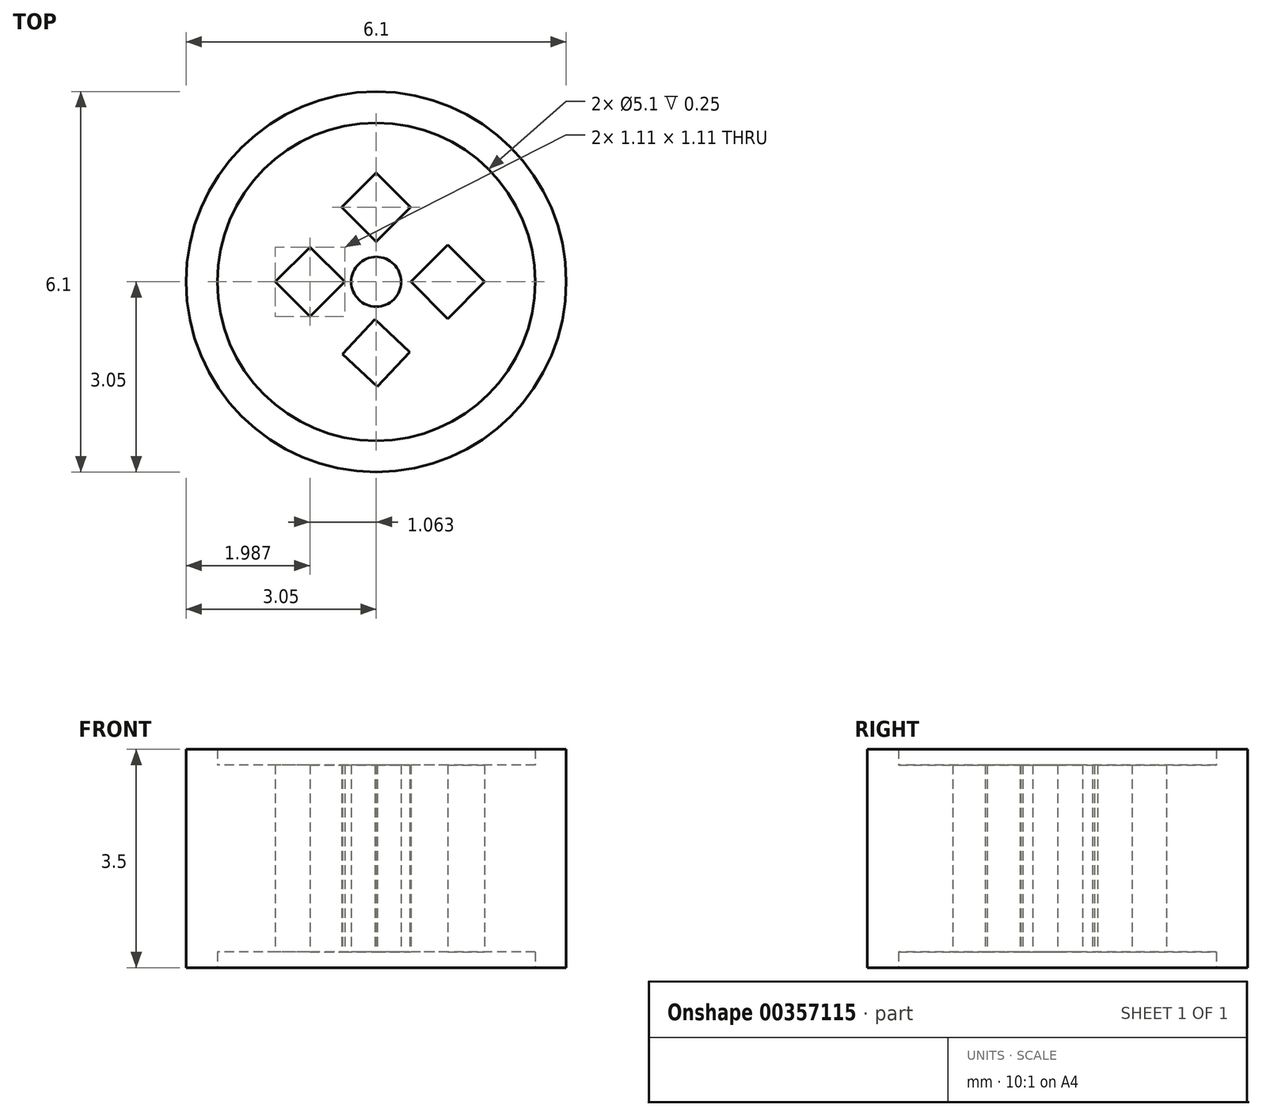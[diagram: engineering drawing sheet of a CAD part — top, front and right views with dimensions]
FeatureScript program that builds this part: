
annotation { "Feature Type Name" : "Feature", "Feature Type Description" : "" }
export const myFeature = defineFeature(function(context is Context, id is Id, definition is map)
    precondition{}
    {
        {
            var Q0;
            Q0=qCreatedBy(makeId("Top.planeOp"),FACE);
            var sketch = newSketch(context, id + "F0", { "sketchPlane" : qUnion([Q0])});
            skCircle(sketch, "E0", {"center": v(0, 0) * mm, "radius": 0.4 * mm});
            skCircle(sketch, "E1", {"center": v(0, 0) * mm, "radius": 2.55 * mm});
            skCircle(sketch, "E2", {"center": v(0, 0) * mm, "radius": 3.05 * mm});
            skLineSegment(sketch, "E3.0", {"start": v(-0.55, 1.2) * mm, "end": v(0, 1.75) * mm});
            skLineSegment(sketch, "E3.1", {"start": v(0, 1.75) * mm, "end": v(0.55, 1.2) * mm});
            skLineSegment(sketch, "E3.2", {"start": v(0.55, 1.2) * mm, "end": v(0, 0.64) * mm});
            skLineSegment(sketch, "E3.3", {"start": v(0, 0.64) * mm, "end": v(-0.55, 1.2) * mm});
            skLineSegment(sketch, "E4.0", {"start": v(-1.62, 0) * mm, "end": v(-1.06, 0.56) * mm});
            skLineSegment(sketch, "E4.1", {"start": v(-1.06, 0.56) * mm, "end": v(-0.5, 0) * mm});
            skLineSegment(sketch, "E4.2", {"start": v(-0.5, 0) * mm, "end": v(-1.06, -0.56) * mm});
            skLineSegment(sketch, "E4.3", {"start": v(-1.06, -0.56) * mm, "end": v(-1.62, 0) * mm});
            skLineSegment(sketch, "E5.0", {"start": v(-0.54, -1.16) * mm, "end": v(-0.02, -0.6) * mm});
            skLineSegment(sketch, "E5.1", {"start": v(-0.02, -0.6) * mm, "end": v(0.54, -1.13) * mm});
            skLineSegment(sketch, "E5.2", {"start": v(0.54, -1.13) * mm, "end": v(0.02, -1.68) * mm});
            skLineSegment(sketch, "E5.3", {"start": v(0.02, -1.68) * mm, "end": v(-0.54, -1.16) * mm});
            skLineSegment(sketch, "E6.0", {"start": v(0.56, 0) * mm, "end": v(1.15, 0.6) * mm});
            skLineSegment(sketch, "E6.1", {"start": v(1.15, 0.6) * mm, "end": v(1.74, 0) * mm});
            skLineSegment(sketch, "E6.2", {"start": v(1.74, 0) * mm, "end": v(1.15, -0.6) * mm});
            skLineSegment(sketch, "E6.3", {"start": v(1.15, -0.6) * mm, "end": v(0.56, 0) * mm});
            skSolve(sketch);
        }
        {
            var Q0;
            Q0=makeQuery(id+"F0.imprint","IMPRINT",FACE,{"disambiguationData":[TD([[makeQuery(id+"F0.imprint","IMPRINT",EDGE,{"derivedFrom":sQuery(id+"F0.wireOp",EDGE,"E0")}),-1.0]])]});
            extrude(context, id + "F1", {"entities" : qUnion([Q0]), "endBound" : BoundingType.SYMMETRIC, "depth" : 3 * mm});
        }
        {
            var Q0;
            Q0=makeQuery(id+"F0.imprint","IMPRINT",FACE,{"disambiguationData":[TD([[makeQuery(id+"F0.imprint","IMPRINT",EDGE,{"derivedFrom":sQuery(id+"F0.wireOp",EDGE,"E1")}),-1.0]])]});
            extrude(context, id + "F2", {"entities" : qUnion([Q0]), "operationType" : NewBodyOperationType.ADD, "endBound" : BoundingType.SYMMETRIC, "depth" : 3.5 * mm});
        }
    });
